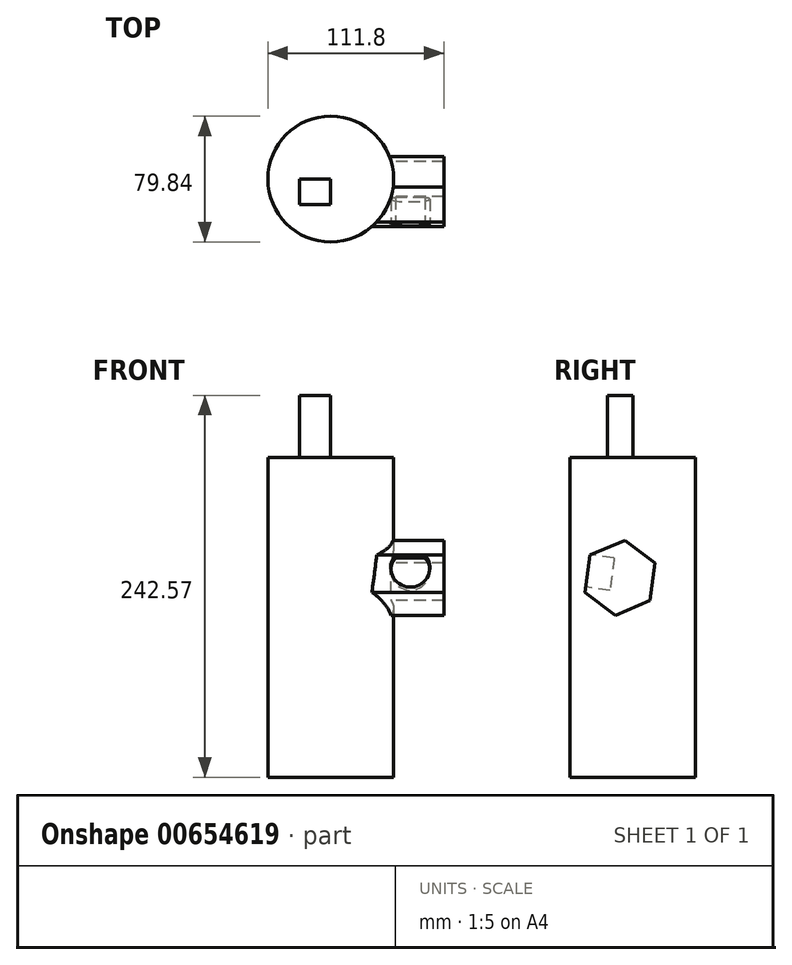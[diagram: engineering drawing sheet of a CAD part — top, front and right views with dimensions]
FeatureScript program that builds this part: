
annotation { "Feature Type Name" : "Feature", "Feature Type Description" : "" }
export const myFeature = defineFeature(function(context is Context, id is Id, definition is map)
    precondition{}
    {
        {
            var Q0;
            Q0=qCreatedBy(makeId("Top.planeOp"),FACE);
            var sketch = newSketch(context, id + "F0", { "sketchPlane" : qUnion([Q0])});
            skCircle(sketch, "E0", {"center": v(0, 0) * mm, "radius": 39.92 * mm});
            skSolve(sketch);
        }
        {
            var Q0;
            Q0 = qSketchRegion(id + "F0", true);
            extrude(context, id + "F1", {"entities" : qUnion([Q0]), "depth" : 203.2 * mm, "offsetDistance" : 25.4 * mm});
        }
        {
            var Q0;
            Q0=makeQuery(id+"F1.opExtrude","CAP_FACE",FACE,{"disambiguationData":[OSD([sQuery(id+"F0.wireOp",EDGE,"E0")])],"isStart":false});
            var sketch = newSketch(context, id + "F2", { "sketchPlane" : qUnion([Q0])});
            skLineSegment(sketch, "E1.bottom", {"start": v(0, 0) * mm, "end": v(-19.82, 0) * mm});
            skLineSegment(sketch, "E1.top", {"start": v(0, -16.08) * mm, "end": v(-19.82, -16.08) * mm});
            skLineSegment(sketch, "E1.left", {"start": v(0, 0) * mm, "end": v(0, -16.08) * mm});
            skLineSegment(sketch, "E1.right", {"start": v(-19.82, 0) * mm, "end": v(-19.82, -16.08) * mm});
            skSolve(sketch);
        }
        {
            var Q0;
            Q0 = qSketchRegion(id + "F2", true);
            extrude(context, id + "F3", {"entities" : qUnion([Q0]), "operationType" : NewBodyOperationType.ADD, "depth" : 39.37 * mm, "offsetDistance" : 25.4 * mm});
        }
        {
            var Q0;
            Q0=makeQuery(id+"F3.opExtrude","SWEPT_FACE",FACE,{"disambiguationData":[OSD([sQuery(id+"F2.wireOp",EDGE,"E1.left")])]});
            var sketch = newSketch(context, id + "F4", { "sketchPlane" : qUnion([Q0])});
            skCircle(sketch, "E2.cCircle", {"center": v(-8.04, 126.74) * mm, "radius": 20.82 * mm, "construction": true});
            skPoint(sketch, "E2.cCircle.centerSnap0", {"position": v(-8.04, 242.57) * mm});
            skLineSegment(sketch, "E2.0", {"start": v(11.09, 112.18) * mm, "end": v(-11.09, 102.9) * mm});
            skLineSegment(sketch, "E2.1", {"start": v(-11.09, 102.9) * mm, "end": v(-30.21, 117.46) * mm});
            skLineSegment(sketch, "E2.2", {"start": v(-30.21, 117.46) * mm, "end": v(-27.16, 141.3) * mm});
            skLineSegment(sketch, "E2.3", {"start": v(-27.16, 141.3) * mm, "end": v(-5, 150.58) * mm});
            skLineSegment(sketch, "E2.4", {"start": v(-5, 150.58) * mm, "end": v(14.13, 136.02) * mm});
            skLineSegment(sketch, "E2.5", {"start": v(14.13, 136.02) * mm, "end": v(11.09, 112.18) * mm});
            skPoint(sketch, "E2.0.midPoint", {"position": v(0, 107.54) * mm});
            skSolve(sketch);
        }
        {
            var Q0;
            Q0 = qSketchRegion(id + "F4", true);
            extrude(context, id + "F5", {"entities" : qUnion([Q0]), "operationType" : NewBodyOperationType.ADD, "depth" : 71.88 * mm, "offsetDistance" : 25.4 * mm});
        }
        {
            var Q0;
            Q0=makeQuery(id+"F5.opExtrude","SWEPT_FACE",FACE,{"disambiguationData":[OSD([sQuery(id+"F4.wireOp",EDGE,"E2.2")])]});
            var sketch = newSketch(context, id + "F6", { "sketchPlane" : qUnion([Q0])});
            skCircle(sketch, "E3", {"center": v(50.57, 128.44) * mm, "radius": 12.43 * mm});
            skPoint(sketch, "E3.centerSnap0", {"position": v(50.57, 136.71) * mm});
            skSolve(sketch);
        }
        {
            var Q0;
            {var subQ0=sQuery(id+"F6.wireOp",EDGE,"E3");var subQ1=makeQuery(id+"F5.opExtrude","SWEPT_EDGE",EDGE,{"disambiguationData":[OSD([sQuery(id+"F4.wireOp",EDGE,"E2.2"),sQuery(id+"F4.wireOp",EDGE,"E2.3")])]});var subQ2=makeQuery(id+"F6.imprint","INTERSECT",VERTEX,{"disambiguationData":[OD(0.0)],"derivedFrom":[subQ1,subQ0]});Q0=makeQuery(id+"F6.imprint","IMPRINT",FACE,{"disambiguationData":[TD([[makeQuery(id+"F6.imprint","IMPRINT",EDGE,{"disambiguationData":[TD([[subQ2,1.0]])],"derivedFrom":subQ0}),1.0]])]});}
            extrude(context, id + "F7", {"entities" : qUnion([Q0]), "operationType" : NewBodyOperationType.REMOVE, "oppositeDirection" : true, "depth" : 15.5 * mm, "offsetDistance" : 25.4 * mm});
        }
    });
